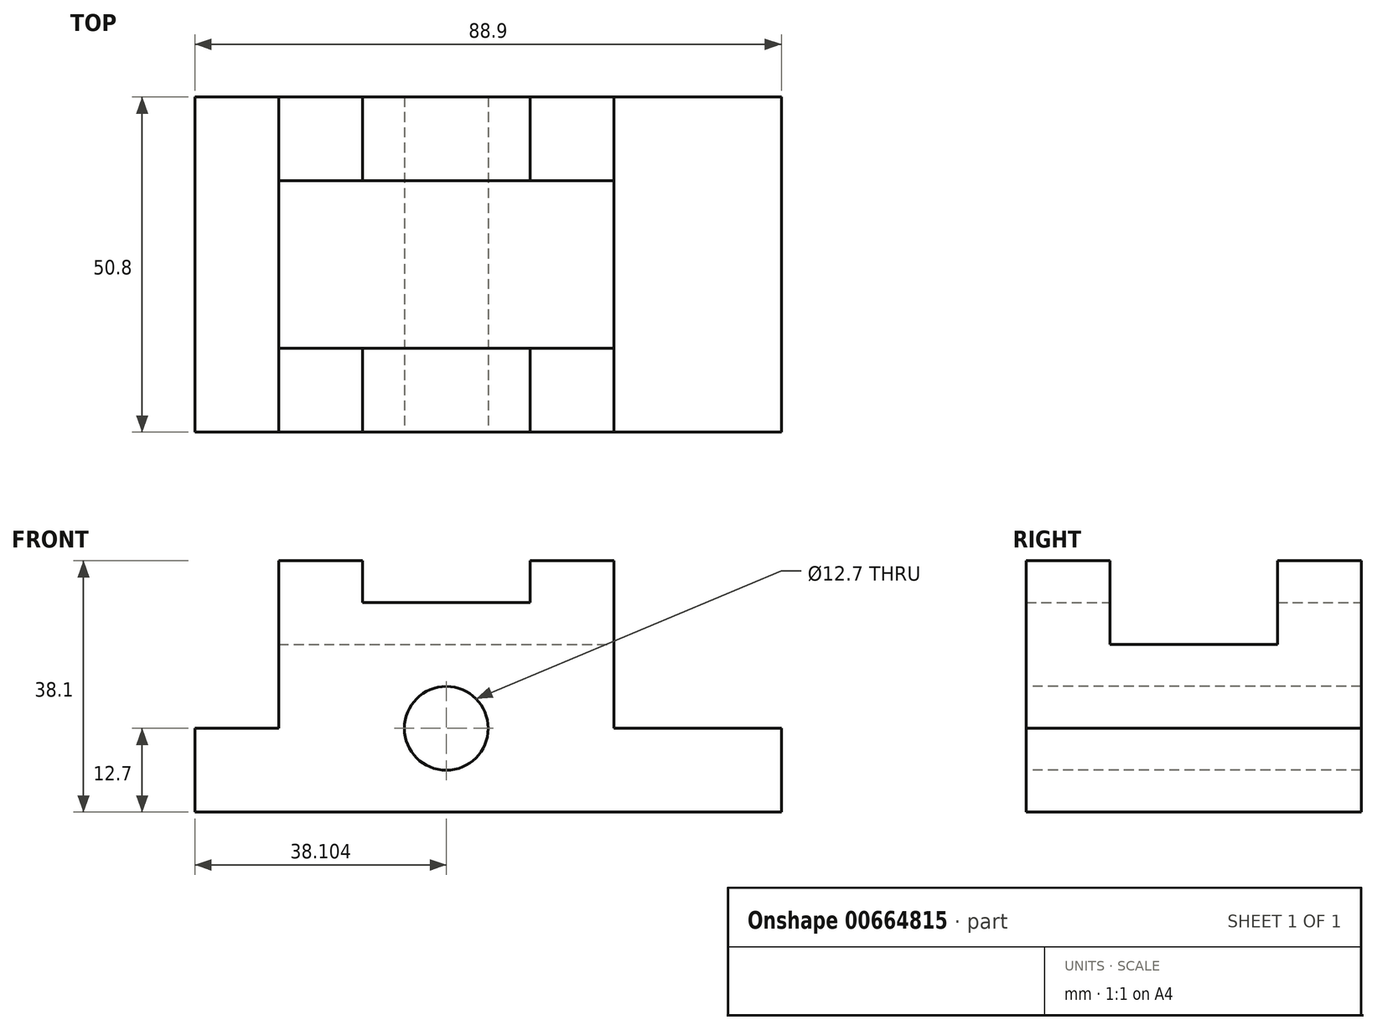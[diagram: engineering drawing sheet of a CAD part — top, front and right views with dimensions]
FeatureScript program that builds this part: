
annotation { "Feature Type Name" : "Feature", "Feature Type Description" : "" }
export const myFeature = defineFeature(function(context is Context, id is Id, definition is map)
    precondition{}
    {
        {
            var Q0;
            Q0=qCreatedBy(makeId("Top.planeOp"),FACE);
            var sketch = newSketch(context, id + "F0", { "sketchPlane" : qUnion([Q0])});
            skLineSegment(sketch, "E0", {"start": v(-59.4, 30) * mm, "end": v(-46.7, 30) * mm});
            skLineSegment(sketch, "E1", {"start": v(-46.7, 30) * mm, "end": v(-46.7, 17.3) * mm});
            skLineSegment(sketch, "E2", {"start": v(-46.7, 17.3) * mm, "end": v(-34, 17.3) * mm});
            skLineSegment(sketch, "E3", {"start": v(-34, 17.3) * mm, "end": v(-34, 30) * mm});
            skLineSegment(sketch, "E4", {"start": v(-34, 30) * mm, "end": v(-46.7, 30) * mm});
            skLineSegment(sketch, "E5", {"start": v(-34, 30) * mm, "end": v(-8.6, 30) * mm});
            skLineSegment(sketch, "E6", {"start": v(-8.6, 30) * mm, "end": v(4.1, 30) * mm});
            skLineSegment(sketch, "E7", {"start": v(4.1, 30) * mm, "end": v(4.1, 17.3) * mm});
            skLineSegment(sketch, "E8", {"start": v(4.1, 17.3) * mm, "end": v(-8.6, 17.3) * mm});
            skLineSegment(sketch, "E9", {"start": v(-8.6, 17.3) * mm, "end": v(-8.6, 30) * mm});
            skLineSegment(sketch, "E10", {"start": v(4.1, 30) * mm, "end": v(29.5, 30) * mm});
            skLineSegment(sketch, "E11", {"start": v(29.5, 30) * mm, "end": v(29.5, -20.8) * mm});
            skLineSegment(sketch, "E12", {"start": v(29.5, -20.8) * mm, "end": v(4.1, -20.8) * mm});
            skLineSegment(sketch, "E13", {"start": v(4.1, -20.8) * mm, "end": v(4.1, -8.1) * mm});
            skLineSegment(sketch, "E14", {"start": v(4.1, -8.1) * mm, "end": v(-8.6, -8.1) * mm});
            skLineSegment(sketch, "E15", {"start": v(-8.6, -8.1) * mm, "end": v(-8.6, -20.8) * mm});
            skLineSegment(sketch, "E16", {"start": v(-8.6, -20.8) * mm, "end": v(-34, -20.8) * mm});
            skLineSegment(sketch, "E17", {"start": v(-34, -20.8) * mm, "end": v(-34, -8.1) * mm});
            skLineSegment(sketch, "E18", {"start": v(-34, -8.1) * mm, "end": v(-46.7, -8.1) * mm});
            skLineSegment(sketch, "E19", {"start": v(-46.7, -8.1) * mm, "end": v(-46.7, -20.8) * mm});
            skLineSegment(sketch, "E20", {"start": v(-46.7, -20.8) * mm, "end": v(-59.4, -20.8) * mm});
            skLineSegment(sketch, "E21", {"start": v(-59.4, -20.8) * mm, "end": v(-59.4, 30) * mm});
            skLineSegment(sketch, "E22", {"start": v(-46.7, -20.8) * mm, "end": v(-34, -20.8) * mm});
            skLineSegment(sketch, "E23", {"start": v(-8.6, -20.8) * mm, "end": v(4.1, -20.8) * mm});
            skLineSegment(sketch, "E24", {"start": v(-8.6, 17.3) * mm, "end": v(-34, 17.3) * mm});
            skLineSegment(sketch, "E25", {"start": v(-34, -8.1) * mm, "end": v(-8.6, -8.1) * mm});
            skLineSegment(sketch, "E26", {"start": v(-46.7, 17.3) * mm, "end": v(-46.7, -8.1) * mm});
            skLineSegment(sketch, "E27", {"start": v(4.1, -8.1) * mm, "end": v(4.1, 17.3) * mm});
            skSolve(sketch);
        }
        {
            var Q0;
            Q0=makeQuery(id+"F0.imprint","IMPRINT",FACE,{"disambiguationData":[TD([[makeQuery(id+"F0.imprint","IMPRINT",EDGE,{"derivedFrom":sQuery(id+"F0.wireOp",EDGE,"E7")}),1.0]])]});
            var Q1;
            Q1=makeQuery(id+"F0.imprint","IMPRINT",FACE,{"disambiguationData":[TD([[makeQuery(id+"F0.imprint","IMPRINT",EDGE,{"derivedFrom":sQuery(id+"F0.wireOp",EDGE,"E0")}),-1.0]])]});
            extrude(context, id + "F1", {"entities" : qUnion([Q0, Q1]), "depth" : 12.7 * mm, "offsetDistance" : 25.4 * mm});
        }
        {
            var Q0;
            Q0=makeQuery(id+"F0.imprint","IMPRINT",FACE,{"disambiguationData":[TD([[makeQuery(id+"F0.imprint","IMPRINT",EDGE,{"derivedFrom":sQuery(id+"F0.wireOp",EDGE,"E2")}),-1.0]])]});
            extrude(context, id + "F2", {"entities" : qUnion([Q0]), "depth" : 25.4 * mm, "offsetDistance" : 25.4 * mm});
        }
        {
            var Q0;
            Q0=makeQuery(id+"F0.imprint","IMPRINT",FACE,{"disambiguationData":[TD([[makeQuery(id+"F0.imprint","IMPRINT",EDGE,{"derivedFrom":sQuery(id+"F0.wireOp",EDGE,"E17")}),1.0]])]});
            var Q1;
            Q1=makeQuery(id+"F0.imprint","IMPRINT",FACE,{"disambiguationData":[TD([[makeQuery(id+"F0.imprint","IMPRINT",EDGE,{"derivedFrom":sQuery(id+"F0.wireOp",EDGE,"E1")}),1.0]])]});
            var Q2;
            Q2=makeQuery(id+"F0.imprint","IMPRINT",FACE,{"disambiguationData":[TD([[makeQuery(id+"F0.imprint","IMPRINT",EDGE,{"derivedFrom":sQuery(id+"F0.wireOp",EDGE,"E6")}),-1.0]])]});
            var Q3;
            Q3=makeQuery(id+"F0.imprint","IMPRINT",FACE,{"disambiguationData":[TD([[makeQuery(id+"F0.imprint","IMPRINT",EDGE,{"derivedFrom":sQuery(id+"F0.wireOp",EDGE,"E13")}),1.0]])]});
            extrude(context, id + "F3", {"entities" : qUnion([Q0, Q1, Q2, Q3]), "depth" : 38.1 * mm, "offsetDistance" : 25.4 * mm});
        }
        {
            var Q0;
            Q0=makeQuery(id+"F0.imprint","IMPRINT",FACE,{"disambiguationData":[TD([[makeQuery(id+"F0.imprint","IMPRINT",EDGE,{"derivedFrom":sQuery(id+"F0.wireOp",EDGE,"E3")}),-1.0]])]});
            var Q1;
            Q1=makeQuery(id+"F0.imprint","IMPRINT",FACE,{"disambiguationData":[TD([[makeQuery(id+"F0.imprint","IMPRINT",EDGE,{"derivedFrom":sQuery(id+"F0.wireOp",EDGE,"E15")}),-1.0]])]});
            extrude(context, id + "F4", {"entities" : qUnion([Q0, Q1]), "depth" : 31.75 * mm, "offsetDistance" : 25.4 * mm});
        }
        {
            var Q0;
            Q0=makeQuery(id+"F1.opExtrude","SWEPT_BODY",BODY,{"disambiguationData":[OSD([sQuery(id+"F0.wireOp",EDGE,"E0"),sQuery(id+"F0.wireOp",EDGE,"E1"),sQuery(id+"F0.wireOp",EDGE,"E19"),sQuery(id+"F0.wireOp",EDGE,"E20"),sQuery(id+"F0.wireOp",EDGE,"E21"),sQuery(id+"F0.wireOp",EDGE,"E26")])]});
            var Q1;
            Q1=makeQuery(id+"F2.opExtrude","SWEPT_BODY",BODY,{"disambiguationData":[OSD([sQuery(id+"F0.wireOp",EDGE,"E2"),sQuery(id+"F0.wireOp",EDGE,"E8"),sQuery(id+"F0.wireOp",EDGE,"E14"),sQuery(id+"F0.wireOp",EDGE,"E18"),sQuery(id+"F0.wireOp",EDGE,"E24"),sQuery(id+"F0.wireOp",EDGE,"E25"),sQuery(id+"F0.wireOp",EDGE,"E26"),sQuery(id+"F0.wireOp",EDGE,"E27")])]});
            var Q2;
            Q2=makeQuery(id+"F3.opExtrude","SWEPT_BODY",BODY,{"disambiguationData":[OSD([sQuery(id+"F0.wireOp",EDGE,"E6"),sQuery(id+"F0.wireOp",EDGE,"E7"),sQuery(id+"F0.wireOp",EDGE,"E8"),sQuery(id+"F0.wireOp",EDGE,"E9")])]});
            var Q3;
            Q3=makeQuery(id+"F3.opExtrude","SWEPT_BODY",BODY,{"disambiguationData":[OSD([sQuery(id+"F0.wireOp",EDGE,"E1"),sQuery(id+"F0.wireOp",EDGE,"E2"),sQuery(id+"F0.wireOp",EDGE,"E3"),sQuery(id+"F0.wireOp",EDGE,"E4")])]});
            var Q4;
            Q4=makeQuery(id+"F4.opExtrude","SWEPT_BODY",BODY,{"disambiguationData":[OSD([sQuery(id+"F0.wireOp",EDGE,"E3"),sQuery(id+"F0.wireOp",EDGE,"E5"),sQuery(id+"F0.wireOp",EDGE,"E9"),sQuery(id+"F0.wireOp",EDGE,"E24")])]});
            var Q5;
            Q5=makeQuery(id+"F3.opExtrude","SWEPT_BODY",BODY,{"disambiguationData":[OSD([sQuery(id+"F0.wireOp",EDGE,"E17"),sQuery(id+"F0.wireOp",EDGE,"E18"),sQuery(id+"F0.wireOp",EDGE,"E19"),sQuery(id+"F0.wireOp",EDGE,"E22")])]});
            var Q6;
            Q6=makeQuery(id+"F3.opExtrude","SWEPT_BODY",BODY,{"disambiguationData":[OSD([sQuery(id+"F0.wireOp",EDGE,"E13"),sQuery(id+"F0.wireOp",EDGE,"E14"),sQuery(id+"F0.wireOp",EDGE,"E15"),sQuery(id+"F0.wireOp",EDGE,"E23")])]});
            var Q7;
            Q7=makeQuery(id+"F4.opExtrude","SWEPT_BODY",BODY,{"disambiguationData":[OSD([sQuery(id+"F0.wireOp",EDGE,"E15"),sQuery(id+"F0.wireOp",EDGE,"E16"),sQuery(id+"F0.wireOp",EDGE,"E17"),sQuery(id+"F0.wireOp",EDGE,"E25")])]});
            var Q8;
            Q8=makeQuery(id+"F1.opExtrude","SWEPT_BODY",BODY,{"disambiguationData":[OSD([sQuery(id+"F0.wireOp",EDGE,"E7"),sQuery(id+"F0.wireOp",EDGE,"E10"),sQuery(id+"F0.wireOp",EDGE,"E11"),sQuery(id+"F0.wireOp",EDGE,"E12"),sQuery(id+"F0.wireOp",EDGE,"E13"),sQuery(id+"F0.wireOp",EDGE,"E27")])]});
            booleanBodies(context, id + "F5", {"operationType" : BooleanOperationType.UNION, "tools" : qUnion([Q0, Q1, Q2, Q3, Q4, Q5, Q6, Q7, Q8])});
        }
        {
            var Q0;
            Q0=makeQuery(id+"F5.opBoolean","MERGE",FACE,{"derivedFrom":[makeQuery(id+"F1.opExtrude","SWEPT_FACE",FACE,{"disambiguationData":[OSD([sQuery(id+"F0.wireOp",EDGE,"E12")])]}),makeQuery(id+"F1.opExtrude","SWEPT_FACE",FACE,{"disambiguationData":[OSD([sQuery(id+"F0.wireOp",EDGE,"E20")])]}),makeQuery(id+"F3.opExtrude","SWEPT_FACE",FACE,{"disambiguationData":[OSD([sQuery(id+"F0.wireOp",EDGE,"E22")])]}),makeQuery(id+"F3.opExtrude","SWEPT_FACE",FACE,{"disambiguationData":[OSD([sQuery(id+"F0.wireOp",EDGE,"E23")])]}),makeQuery(id+"F4.opExtrude","SWEPT_FACE",FACE,{"disambiguationData":[OSD([sQuery(id+"F0.wireOp",EDGE,"E16")])]})]});
            var sketch = newSketch(context, id + "F6", { "sketchPlane" : qUnion([Q0])});
            skCircle(sketch, "E28", {"center": v(-21.3, 12.7) * mm, "radius": 6.35 * mm});
            skSolve(sketch);
        }
        {
            var Q0;
            Q0=sQuery(id+"F6.wireOp",VERTEX,"E28.center");
            var Q1;
            Q1=makeQuery(id+"F1.opExtrude","SWEPT_BODY",BODY,{"disambiguationData":[OSD([sQuery(id+"F0.wireOp",EDGE,"E0"),sQuery(id+"F0.wireOp",EDGE,"E1"),sQuery(id+"F0.wireOp",EDGE,"E19"),sQuery(id+"F0.wireOp",EDGE,"E20"),sQuery(id+"F0.wireOp",EDGE,"E21"),sQuery(id+"F0.wireOp",EDGE,"E26")])]});
            hole(context, id + "F7", {"style" : HoleStyle.SIMPLE, "endStyle" : HoleEndStyle.THROUGH, "holeDiameter" : 12.7 * mm, "majorDiameter" : 6.35 * mm, "isTappedThrough" : true, "tappedDepth" : 12.7 * mm, "tapClearance" : 3, "locations" : qUnion([Q0]), "scope" : qUnion([Q1])});
        }
    });
